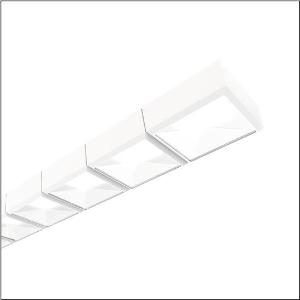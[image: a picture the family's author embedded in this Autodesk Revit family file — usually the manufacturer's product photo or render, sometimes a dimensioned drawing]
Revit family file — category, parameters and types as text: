
# Revit family: scriptus_r__11_5mz312d0twb_510a
name_source: partatom
category: Lighting Fixtures
units: mm (PartAtom-declared; Revit-internal decimal feet)

## family parameters
Cut with Voids When Loaded = No
Host = Face
Light Source = No
Part Type = Normal
Room Calculation Point = No
Round Connector Dimension = Use Diameter
Shared = No

## types (1)
- --- (1 x LED 3000K+6500K / CRI = 80 (unbekannt), 3200 lm / 2380 lm, 3000K)
    Apparent Load = 94 VA
    CIE Flux Codes = 0 0 0 0 100 / 82 95 99 100 100
    Color Rendering = 80
    Color Temperature = 3000K
    Default Elevation = 1800 mm
    Description = Scriptus® 11, office luminaire, primary optical cover: lenses, CAT 2 (L<= 3000cd/m²), light emission: direct/indirect distribution, primary light characteristic: symmetric, installation type: suspended mounting, LED, rated luminous flux: 11.150lm, luminous efficacy: 116lm/W, light colour: 8tw, colour temperature: 3000..6500K, control gear: ECG DALI, with terminal, 5-pole, mains connection: 230V, AC, 50Hz, rated input power: 96W, LED, control gear: ECG DALI, housing, luminaire housing, of aluminium, traffic white (RAL 9016), length: 1.768mm, width: 114mm, height: 57mm, protection rating (complete): IP20, insulation class (complete): insulation class I (protective earthing), certification: CE, protection symbol: F, permissible operating ambient temperature: <= +25°C, standard: EN 50419, packaging unit: 1 piece
    Height = 57 mm
    Lamp = 1 x LED 3000K+6500K / CRI >= 80 (unbekannt)
    Lamp Light Flux = 3200 lm / 2380 lm
    Lamp count = 1
    Length = 1768 mm
    Luminous efficacy = 119 lm/W
    Manufacturer = Siteco
    ModVariant = No
    Model = 5MZ312D0TWB
    Mounting Place = Ceiling
    Mounting Type = Pendant
    Number of Poles = 1
    OnlyDefault = Yes
    Power Factor = 1
    Product Name = Scriptus® 11
    Product group = office luminaire | ceiling pendant
    ProductGroupID = 902
    Protection Class = Protection class I
    Protection Degree = IP 20
    RLX_Detail_Level = 1
    RLX_Emergency_Light_Flux = 0 lm
    RLX_Emergency_Type = 0
    RLX_Emergency_Type_DB = No
    RlxData = <blob elided: 31681 chars, md5=7b40fb49>
    Socket = socket
    Standby Power = 0 W
    System Light Flux = 11160 lm
    System Power = 94 W
    Type Comments = individual setting: colour temperature 6500K
    Type Image = l_1004839.jpg
    URL = http://relux.com
    VarID = @adj_179504
    Voltage = 0 V
    Weight = 0.00 kg
    Width = 114 mm

## geometry (parser evidence)
native form markers: Blend x4, Sweep x19
no freeform markers — native parametric forms only
